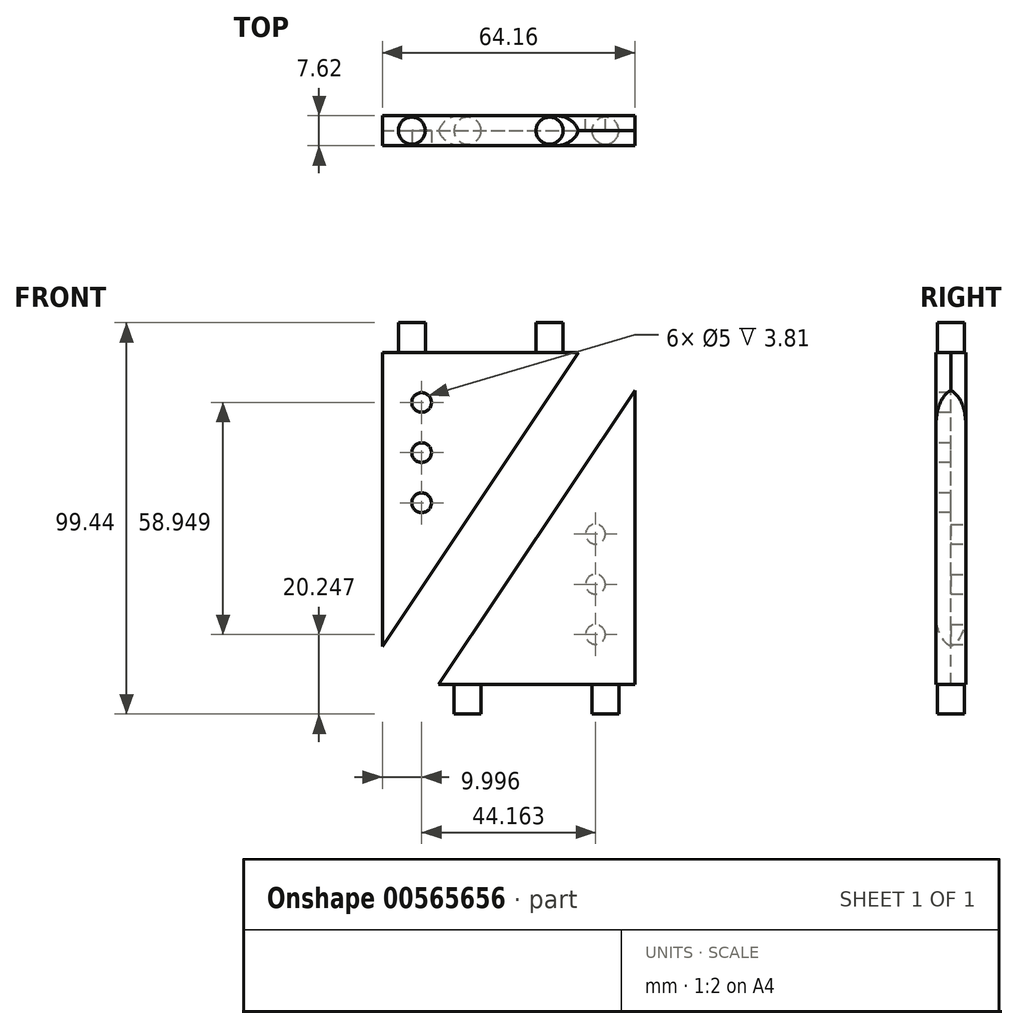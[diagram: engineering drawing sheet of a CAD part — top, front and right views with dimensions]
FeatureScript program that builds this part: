
annotation { "Feature Type Name" : "Feature", "Feature Type Description" : "" }
export const myFeature = defineFeature(function(context is Context, id is Id, definition is map)
    precondition{}
    {
        {
            var Q0;
            Q0=qCreatedBy(makeId("Front.planeOp"),FACE);
            var sketch = newSketch(context, id + "F0", { "sketchPlane" : qUnion([Q0])});
            skLineSegment(sketch, "E0.top", {"start": v(-25, -37.5) * mm, "end": v(25, -37.5) * mm});
            skLineSegment(sketch, "E0.right", {"start": v(25, 37.5) * mm, "end": v(25, -37.5) * mm});
            skPoint(sketch, "E0.middle", {"position": v(0, 0) * mm});
            skLineSegment(sketch, "E1", {"start": v(-25, -37.5) * mm, "end": v(25, 37.5) * mm});
            skLineSegment(sketch, "E2.top", {"start": v(10.84, 46.94) * mm, "end": v(-39.16, 46.94) * mm});
            skLineSegment(sketch, "E2.right", {"start": v(-39.16, -28.06) * mm, "end": v(-39.16, 46.94) * mm});
            skPoint(sketch, "E2.middle", {"position": v(-14.16, 9.44) * mm});
            skLineSegment(sketch, "E3", {"start": v(10.84, 46.94) * mm, "end": v(-39.16, -28.06) * mm});
            skLineSegment(sketch, "E4", {"start": v(-14.16, 9.44) * mm, "end": v(0, 0) * mm, "construction": true});
            skLineSegment(sketch, "E5", {"start": v(-39.16, -28.06) * mm, "end": v(-25, -37.5) * mm, "construction": true});
            skLineSegment(sketch, "E6", {"start": v(10.84, 46.94) * mm, "end": v(25, 37.5) * mm, "construction": true});
            skSolve(sketch);
        }
        {
            var Q0;
            Q0=makeQuery(id+"F0.imprint","IMPRINT",FACE,{"disambiguationData":[TD([[makeQuery(id+"F0.imprint","IMPRINT",EDGE,{"derivedFrom":sQuery(id+"F0.wireOp",EDGE,"E0.top")}),1.0]])]});
            var Q1;
            Q1=makeQuery(id+"F0.imprint","IMPRINT",FACE,{"disambiguationData":[TD([[makeQuery(id+"F0.imprint","IMPRINT",EDGE,{"derivedFrom":sQuery(id+"F0.wireOp",EDGE,"E2.top")}),1.0]])]});
            extrude(context, id + "F1", {"entities" : qUnion([Q0, Q1]), "depth" : 7.62 * mm, "offsetDistance" : 25 * mm});
        }
        {
            var Q0;
            Q0=makeQuery(id+"F1.opExtrude","SWEPT_FACE",FACE,{"disambiguationData":[OSD([sQuery(id+"F0.wireOp",EDGE,"E2.top")])]});
            var sketch = newSketch(context, id + "F2", { "sketchPlane" : qUnion([Q0])});
            skCircle(sketch, "E7", {"center": v(-31.66, -3.81) * mm, "radius": 3.43 * mm});
            skCircle(sketch, "E8", {"center": v(3.34, -3.81) * mm, "radius": 3.43 * mm});
            skLineSegment(sketch, "E9", {"start": v(-31.66, -3.81) * mm, "end": v(3.34, -3.81) * mm, "construction": true});
            skLineSegment(sketch, "E10", {"start": v(-31.66, -3.81) * mm, "end": v(-39.16, -3.81) * mm, "construction": true});
            skLineSegment(sketch, "E11", {"start": v(3.34, -3.81) * mm, "end": v(10.84, -3.81) * mm, "construction": true});
            skLineSegment(sketch, "E12", {"start": v(-14.16, 0) * mm, "end": v(-14.16, -7.62) * mm, "construction": true});
            skSolve(sketch);
        }
        {
            var Q0;
            Q0=makeQuery(id+"F1.opExtrude","SWEPT_FACE",FACE,{"disambiguationData":[OSD([sQuery(id+"F0.wireOp",EDGE,"E0.top")])]});
            var sketch = newSketch(context, id + "F3", { "sketchPlane" : qUnion([Q0])});
            skLineSegment(sketch, "E13", {"start": v(0, 7.62) * mm, "end": v(0, 0) * mm, "construction": true});
            skCircle(sketch, "E14", {"center": v(-17.5, 3.8) * mm, "radius": 3.43 * mm});
            skCircle(sketch, "E15", {"center": v(17.5, 3.8) * mm, "radius": 3.43 * mm});
            skLineSegment(sketch, "E16", {"start": v(-17.5, 3.81) * mm, "end": v(17.5, 3.81) * mm, "construction": true});
            skLineSegment(sketch, "E17", {"start": v(-17.5, 3.81) * mm, "end": v(-25, 3.81) * mm, "construction": true});
            skLineSegment(sketch, "E18", {"start": v(17.5, 3.81) * mm, "end": v(25, 3.81) * mm, "construction": true});
            skSolve(sketch);
        }
        {
            var Q0;
            Q0=makeQuery(id+"F2.imprint","IMPRINT",FACE,{"disambiguationData":[TD([[makeQuery(id+"F2.imprint","IMPRINT",EDGE,{"derivedFrom":sQuery(id+"F2.wireOp",EDGE,"E7")}),1.0]])]});
            var Q1;
            Q1=makeQuery(id+"F2.imprint","IMPRINT",FACE,{"disambiguationData":[TD([[makeQuery(id+"F2.imprint","IMPRINT",EDGE,{"derivedFrom":sQuery(id+"F2.wireOp",EDGE,"E8")}),1.0]])]});
            extrude(context, id + "F4", {"entities" : qUnion([Q0, Q1]), "operationType" : NewBodyOperationType.ADD, "depth" : (15 / 2) * mm, "offsetDistance" : 25 * mm});
        }
        {
            var Q0;
            Q0=makeQuery(id+"F3.imprint","IMPRINT",FACE,{"disambiguationData":[TD([[makeQuery(id+"F3.imprint","IMPRINT",EDGE,{"derivedFrom":sQuery(id+"F3.wireOp",EDGE,"E14")}),1.0]])]});
            var Q1;
            Q1=makeQuery(id+"F3.imprint","IMPRINT",FACE,{"disambiguationData":[TD([[makeQuery(id+"F3.imprint","IMPRINT",EDGE,{"derivedFrom":sQuery(id+"F3.wireOp",EDGE,"E15")}),1.0]])]});
            extrude(context, id + "F5", {"entities" : qUnion([Q0, Q1]), "operationType" : NewBodyOperationType.ADD, "depth" : (15 / 2) * mm, "offsetDistance" : 25 * mm});
        }
        {
            var Q0;
            Q0=makeQuery(id+"F1.opExtrude","CAP_EDGE",EDGE,{"disambiguationData":[OSD([sQuery(id+"F0.wireOp",EDGE,"E1")])],"isStart":false});
            var Q1;
            Q1=makeQuery(id+"F1.opExtrude","CAP_EDGE",EDGE,{"disambiguationData":[OSD([sQuery(id+"F0.wireOp",EDGE,"E1")])],"isStart":true});
            var Q2;
            Q2=makeQuery(id+"F1.opExtrude","CAP_EDGE",EDGE,{"disambiguationData":[OSD([sQuery(id+"F0.wireOp",EDGE,"E3")])],"isStart":true});
            var Q3;
            Q3=makeQuery(id+"F1.opExtrude","CAP_EDGE",EDGE,{"disambiguationData":[OSD([sQuery(id+"F0.wireOp",EDGE,"E3")])],"isStart":false});
            fillet(context, id + "F6", {"entities" : qUnion([Q0, Q1, Q2, Q3]), "radius" : 5 * mm, "tangentPropagation" : true, "allowEdgeOverflow" : false});
        }
        {
            var Q0;
            Q0=makeQuery(id+"F1.opExtrude","CAP_FACE",FACE,{"disambiguationData":[OSD([sQuery(id+"F0.wireOp",EDGE,"E0.top"),sQuery(id+"F0.wireOp",EDGE,"E0.right"),sQuery(id+"F0.wireOp",EDGE,"E1")])],"isStart":true});
            var sketch = newSketch(context, id + "F7", { "sketchPlane" : qUnion([Q0])});
            skLineSegment(sketch, "E19", {"start": v(-25, 28.49) * mm, "end": v(-25, -37.5) * mm, "construction": true});
            skLineSegment(sketch, "E20.0", {"start": v(-15, 13.49) * mm, "end": v(-15, -37.5) * mm, "construction": true});
            skCircle(sketch, "E21", {"center": v(-15, 0.74) * mm, "radius": 2.5 * mm});
            skCircle(sketch, "E22", {"center": v(-15, -12) * mm, "radius": 2.5 * mm});
            skCircle(sketch, "E23", {"center": v(-15, -24.75) * mm, "radius": 2.5 * mm});
            skLineSegment(sketch, "E24", {"start": v(-15, 0.74) * mm, "end": v(-15, -12) * mm, "construction": true});
            skLineSegment(sketch, "E25", {"start": v(-15, -12) * mm, "end": v(-15, -24.75) * mm, "construction": true});
            skLineSegment(sketch, "E26", {"start": v(-15, -24.75) * mm, "end": v(-15, -37.5) * mm, "construction": true});
            skLineSegment(sketch, "E27", {"start": v(-15, 0.74) * mm, "end": v(-15, 13.49) * mm, "construction": true});
            skSolve(sketch);
        }
        {
            var Q0;
            Q0=makeQuery(id+"F1.opExtrude","CAP_FACE",FACE,{"disambiguationData":[OSD([sQuery(id+"F0.wireOp",EDGE,"E2.top"),sQuery(id+"F0.wireOp",EDGE,"E2.right"),sQuery(id+"F0.wireOp",EDGE,"E3")])],"isStart":false});
            var sketch = newSketch(context, id + "F8", { "sketchPlane" : qUnion([Q0])});
            skLineSegment(sketch, "E28", {"start": v(-39.16, 46.94) * mm, "end": v(-39.16, -19.04) * mm, "construction": true});
            skLineSegment(sketch, "E29.0", {"start": v(-29.16, 46.94) * mm, "end": v(-29.16, -4.04) * mm, "construction": true});
            skCircle(sketch, "E30", {"center": v(-29.16, 34.2) * mm, "radius": 2.5 * mm});
            skCircle(sketch, "E31", {"center": v(-29.16, 21.45) * mm, "radius": 2.5 * mm});
            skCircle(sketch, "E32", {"center": v(-29.16, 8.7) * mm, "radius": 2.5 * mm});
            skLineSegment(sketch, "E33", {"start": v(-29.16, 34.2) * mm, "end": v(-29.16, 21.45) * mm, "construction": true});
            skLineSegment(sketch, "E34", {"start": v(-29.16, 21.45) * mm, "end": v(-29.16, 8.7) * mm, "construction": true});
            skLineSegment(sketch, "E35", {"start": v(-29.16, 8.7) * mm, "end": v(-29.16, -4.04) * mm, "construction": true});
            skLineSegment(sketch, "E36", {"start": v(-29.16, 34.2) * mm, "end": v(-29.16, 46.94) * mm, "construction": true});
            skSolve(sketch);
        }
        {
            var Q0;
            Q0=makeQuery(id+"F7.imprint","IMPRINT",FACE,{"disambiguationData":[TD([[makeQuery(id+"F7.imprint","IMPRINT",EDGE,{"derivedFrom":sQuery(id+"F7.wireOp",EDGE,"E23")}),1.0]])]});
            var Q1;
            Q1=makeQuery(id+"F7.imprint","IMPRINT",FACE,{"disambiguationData":[TD([[makeQuery(id+"F7.imprint","IMPRINT",EDGE,{"derivedFrom":sQuery(id+"F7.wireOp",EDGE,"E22")}),1.0]])]});
            var Q2;
            Q2=makeQuery(id+"F7.imprint","IMPRINT",FACE,{"disambiguationData":[TD([[makeQuery(id+"F7.imprint","IMPRINT",EDGE,{"derivedFrom":sQuery(id+"F7.wireOp",EDGE,"E21")}),1.0]])]});
            extrude(context, id + "F9", {"entities" : qUnion([Q0, Q1, Q2]), "operationType" : NewBodyOperationType.REMOVE, "oppositeDirection" : true, "depth" : 3.8 * mm, "offsetDistance" : 25 * mm});
        }
        {
            var Q0;
            Q0=makeQuery(id+"F8.imprint","IMPRINT",FACE,{"disambiguationData":[TD([[makeQuery(id+"F8.imprint","IMPRINT",EDGE,{"derivedFrom":sQuery(id+"F8.wireOp",EDGE,"E32")}),1.0]])]});
            var Q1;
            Q1=makeQuery(id+"F8.imprint","IMPRINT",FACE,{"disambiguationData":[TD([[makeQuery(id+"F8.imprint","IMPRINT",EDGE,{"derivedFrom":sQuery(id+"F8.wireOp",EDGE,"E31")}),1.0]])]});
            var Q2;
            Q2=makeQuery(id+"F8.imprint","IMPRINT",FACE,{"disambiguationData":[TD([[makeQuery(id+"F8.imprint","IMPRINT",EDGE,{"derivedFrom":sQuery(id+"F8.wireOp",EDGE,"E30")}),1.0]])]});
            extrude(context, id + "F10", {"entities" : qUnion([Q0, Q1, Q2]), "operationType" : NewBodyOperationType.REMOVE, "oppositeDirection" : true, "depth" : 3.8 * mm, "offsetDistance" : 25 * mm});
        }
    });
